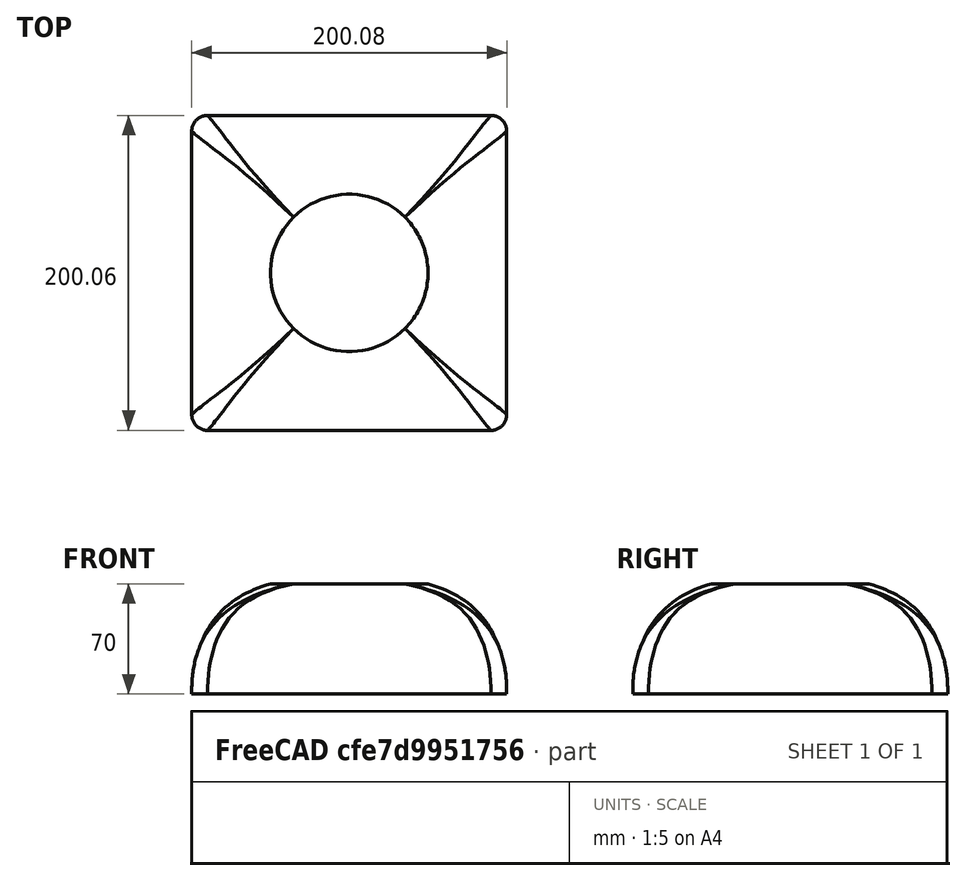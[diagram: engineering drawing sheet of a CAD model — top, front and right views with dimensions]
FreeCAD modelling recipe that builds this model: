
FCSTD DOCUMENT  (FreeCAD 0.15R4671 (Git))
Label: mark2
License: All rights reserved
LicenseURL: http://en.wikipedia.org/wiki/All_rights_reserved
objects: Sketcher::SketchObject×3, Part::Loft×1, PartDesign::Fillet×1
note: 5 computed .brp shape members not serialized (recipe doc carries the construction recipe); baked Part::Feature solids carry a one-line shape summary decoded from their .brp

FEATURE [Sketcher::SketchObject] Sketch001  label="kuklos2"
  Placement = pos=(0,0,-20) rot=(0,0,1;0rad)
  sketch-geometry (1):
    g0: Circle CenterX=0 CenterY=0 CenterZ=0 NormalX=0 NormalY=0 NormalZ=1 Radius=50
  constraints (2):
    c: Coincident(g0,g-1)
    c: Radius(g0) = 50
FEATURE [Sketcher::SketchObject] Sketch002  label="tetragwno"
  Placement = pos=(0,0,-60) rot=(0,0,1;0rad)
  sketch-geometry (4):
    g0: LineSegment StartX=-95 StartY=95 StartZ=0 EndX=95 EndY=95 EndZ=0
    g1: LineSegment StartX=95 StartY=95 StartZ=0 EndX=95 EndY=-95 EndZ=0
    g2: LineSegment StartX=95 StartY=-95 StartZ=0 EndX=-95 EndY=-95 EndZ=0
    g3: LineSegment StartX=-95 StartY=-95 StartZ=0 EndX=-95 EndY=95 EndZ=0
  constraints (12):
    c: Coincident(g0,g1)
    c: Coincident(g1,g2)
    c: Coincident(g2,g3)
    c: Coincident(g3,g0)
    c: Horizontal(g0)
    c: Horizontal(g2)
    c: Vertical(g1)
    c: Vertical(g3)
    c: Equal(g0,g3)
    c: Symmetric(g0,g0,g-2)
    c: Symmetric(g0,g2,g-1)
    c: DistanceY(g3) = 190
FEATURE [Sketcher::SketchObject] Sketch003  label="tetragwno001"
  Placement = pos=(0,0,-90) rot=(0,0,1;0rad)
  sketch-geometry (4):
    g0: LineSegment StartX=-100 StartY=100 StartZ=0 EndX=100 EndY=100 EndZ=0
    g1: LineSegment StartX=100 StartY=100 StartZ=0 EndX=100 EndY=-100 EndZ=0
    g2: LineSegment StartX=100 StartY=-100 StartZ=0 EndX=-100 EndY=-100 EndZ=0
    g3: LineSegment StartX=-100 StartY=-100 StartZ=0 EndX=-100 EndY=100 EndZ=0
  constraints (12):
    c: Coincident(g0,g1)
    c: Coincident(g1,g2)
    c: Coincident(g2,g3)
    c: Coincident(g3,g0)
    c: Horizontal(g0)
    c: Horizontal(g2)
    c: Vertical(g1)
    c: Vertical(g3)
    c: Equal(g0,g3)
    c: Symmetric(g0,g0,g-2)
    c: Symmetric(g0,g2,g-1)
    c: DistanceY(g3) = 200
FEATURE [Part::Loft] Loft
  Closed = false
  Ruled = false
  Sections = -> [Sketch003,Sketch002,Sketch001]
  Solid = false
FEATURE [PartDesign::Fillet] Fillet
  Base = -> Loft [Edge4,Edge2,Edge9,Edge12]
  Radius = 10
